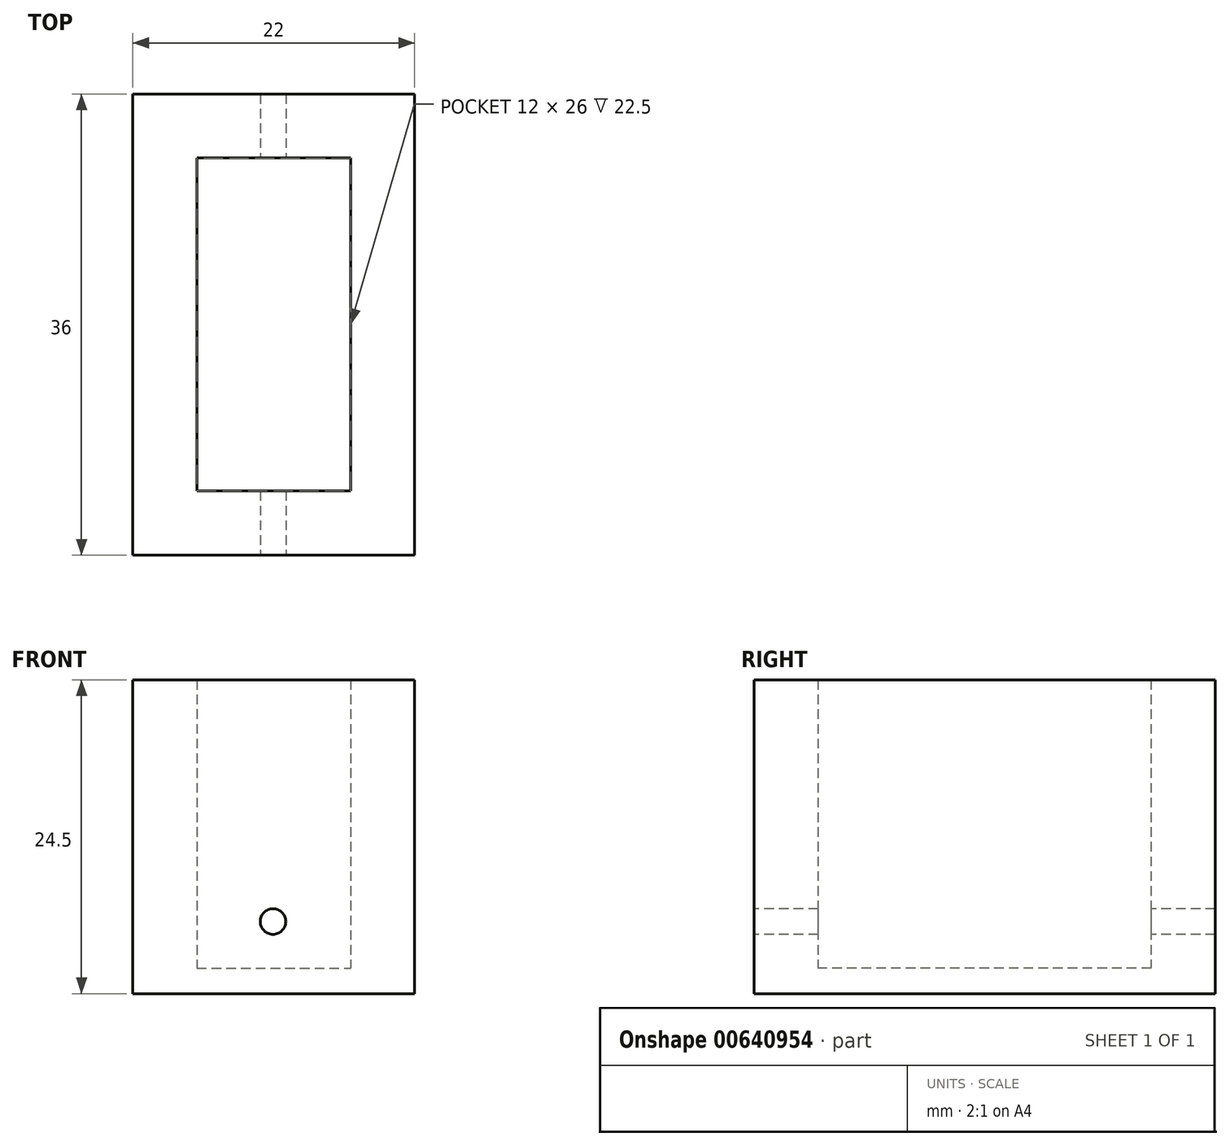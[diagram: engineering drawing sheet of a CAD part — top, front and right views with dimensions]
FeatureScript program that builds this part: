
annotation { "Feature Type Name" : "Feature", "Feature Type Description" : "" }
export const myFeature = defineFeature(function(context is Context, id is Id, definition is map)
    precondition{}
    {
        {
            var Q0;
            Q0=qCreatedBy(makeId("Top.planeOp"),FACE);
            var sketch = newSketch(context, id + "F0", { "sketchPlane" : qUnion([Q0])});
            skLineSegment(sketch, "E0.bottom", {"start": v(0, 0) * mm, "end": v(12, 0) * mm});
            skLineSegment(sketch, "E0.top", {"start": v(0, -26) * mm, "end": v(12, -26) * mm});
            skLineSegment(sketch, "E0.left", {"start": v(0, 0) * mm, "end": v(0, -26) * mm});
            skLineSegment(sketch, "E0.right", {"start": v(12, 0) * mm, "end": v(12, -26) * mm});
            skLineSegment(sketch, "E1.0", {"start": v(17, 5) * mm, "end": v(17, -31) * mm});
            skLineSegment(sketch, "E1.1", {"start": v(-5, 5) * mm, "end": v(17, 5) * mm});
            skLineSegment(sketch, "E1.2", {"start": v(-5, 5) * mm, "end": v(-5, -31) * mm});
            skLineSegment(sketch, "E1.3", {"start": v(-5, -31) * mm, "end": v(17, -31) * mm});
            skSolve(sketch);
        }
        {
            var Q0;
            Q0=makeQuery(id+"F0.imprint","IMPRINT",FACE,{"disambiguationData":[TD([[makeQuery(id+"F0.imprint","IMPRINT",EDGE,{"derivedFrom":sQuery(id+"F0.wireOp",EDGE,"E0.bottom")}),1.0]])]});
            extrude(context, id + "F1", {"entities" : qUnion([Q0]), "depth" : 24.5 * mm, "offsetDistance" : 25 * mm});
        }
        {
            var Q0;
            Q0=makeQuery(id+"F0.imprint","IMPRINT",FACE,{"disambiguationData":[TD([[makeQuery(id+"F0.imprint","IMPRINT",EDGE,{"derivedFrom":sQuery(id+"F0.wireOp",EDGE,"E0.bottom")}),-1.0]])]});
            extrude(context, id + "F2", {"entities" : qUnion([Q0]), "operationType" : NewBodyOperationType.ADD, "depth" : 2 * mm, "offsetDistance" : 25 * mm});
        }
        {
            var Q0;
            Q0=makeQuery(id+"F1.opExtrude","SWEPT_FACE",FACE,{"disambiguationData":[OSD([sQuery(id+"F0.wireOp",EDGE,"E1.3")])]});
            var sketch = newSketch(context, id + "F3", { "sketchPlane" : qUnion([Q0])});
            skCircle(sketch, "E2", {"center": v(5.95, 5.63) * mm, "radius": 1 * mm});
            skSolve(sketch);
        }
        {
            var Q0;
            Q0=makeQuery(id+"F3.imprint","IMPRINT",FACE,{"disambiguationData":[TD([[makeQuery(id+"F3.imprint","IMPRINT",EDGE,{"derivedFrom":sQuery(id+"F3.wireOp",EDGE,"E2")}),1.0]])]});
            extrude(context, id + "F4", {"entities" : qUnion([Q0]), "operationType" : NewBodyOperationType.REMOVE, "endBound" : BoundingType.THROUGH_ALL, "oppositeDirection" : true, "depth" : 25 * mm, "offsetDistance" : 25 * mm});
        }
    });
